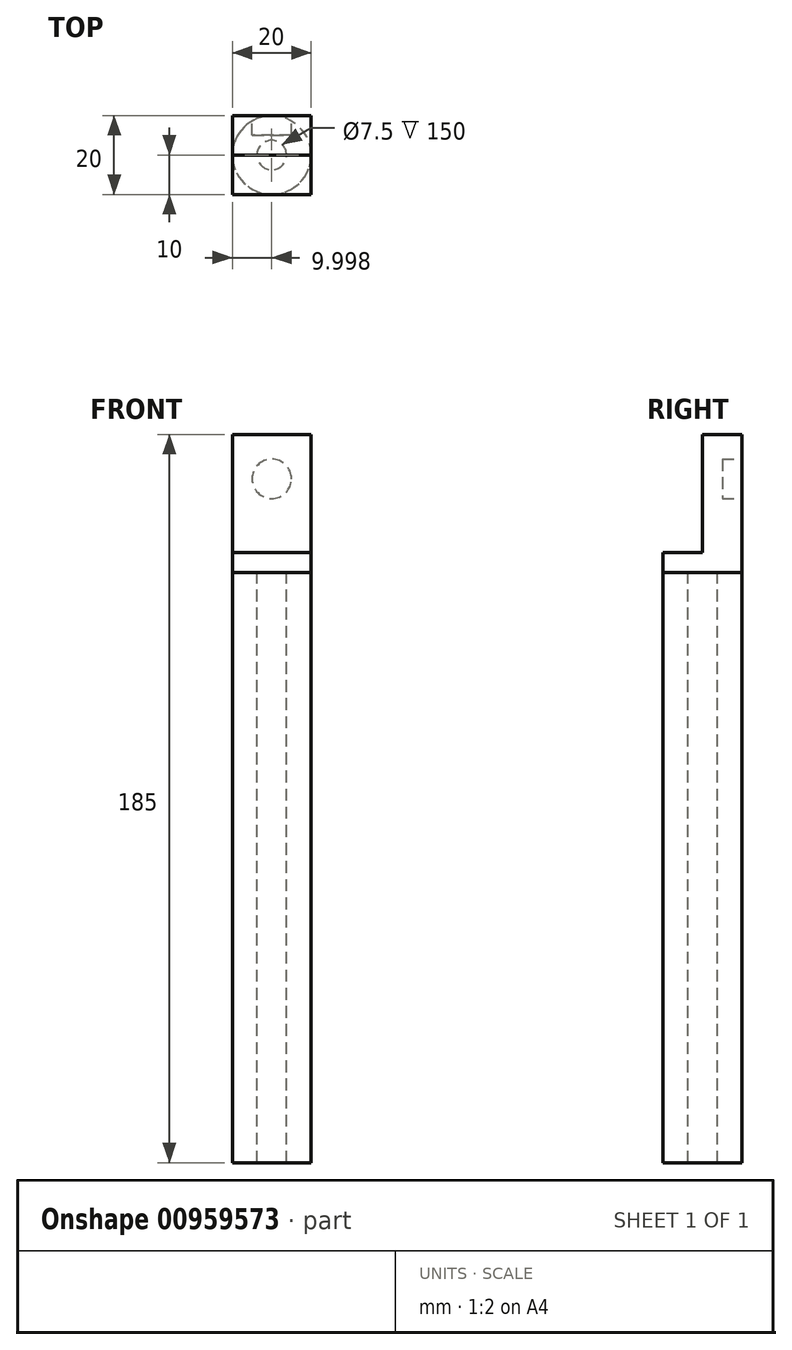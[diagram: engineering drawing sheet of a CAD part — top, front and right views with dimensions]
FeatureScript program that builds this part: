
annotation { "Feature Type Name" : "Feature", "Feature Type Description" : "" }
export const myFeature = defineFeature(function(context is Context, id is Id, definition is map)
    precondition{}
    {
        {
            var Q0;
            Q0=qCreatedBy(makeId("Top.planeOp"),FACE);
            var sketch = newSketch(context, id + "F0", { "sketchPlane" : qUnion([Q0])});
            skLineSegment(sketch, "E0", {"start": v(-66.14, 69.13) * mm, "end": v(-46.14, 69.13) * mm});
            skLineSegment(sketch, "E1", {"start": v(-66.14, 69.13) * mm, "end": v(-66.14, 49.13) * mm});
            skLineSegment(sketch, "E2", {"start": v(-66.14, 49.13) * mm, "end": v(-46.14, 49.13) * mm});
            skLineSegment(sketch, "E3", {"start": v(-46.14, 69.13) * mm, "end": v(-46.14, 49.13) * mm});
            skSolve(sketch);
        }
        {
            var Q0;
            Q0 = qSketchRegion(id + "F0", true);
            var Q1;
            Q1=makeQuery(id+"F0.imprint","IMPRINT",FACE,{"disambiguationData":[TD([[makeQuery(id+"F0.imprint","IMPRINT",EDGE,{"derivedFrom":sQuery(id+"F0.wireOp",EDGE,"E0")}),-1.0]])]});
            extrude(context, id + "F1", {"entities" : qUnion([Q0, Q1]), "depth" : 5 * mm, "offsetDistance" : 25 * mm});
        }
        {
            var Q0;
            Q0=makeQuery(id+"F1.opExtrude","CAP_FACE",FACE,{"disambiguationData":[OSD([sQuery(id+"F0.wireOp",EDGE,"E0"),sQuery(id+"F0.wireOp",EDGE,"E1"),sQuery(id+"F0.wireOp",EDGE,"E2"),sQuery(id+"F0.wireOp",EDGE,"E3")])],"isStart":true});
            var sketch = newSketch(context, id + "F2", { "sketchPlane" : qUnion([Q0])});
            skCircle(sketch, "E4", {"center": v(-56.14, -59.13) * mm, "radius": 10 * mm});
            skPoint(sketch, "E4.first.point", {"position": v(-56.14, -49.13) * mm});
            skPoint(sketch, "E4.second.point", {"position": v(-56.14, -69.13) * mm});
            skPoint(sketch, "E4.third.point", {"position": v(-46.14, -59.13) * mm});
            skCircle(sketch, "E5", {"center": v(-56.14, -59.13) * mm, "radius": 3.75 * mm});
            skSolve(sketch);
        }
        {
            var Q0;
            Q0=makeQuery(id+"F2.imprint","IMPRINT",FACE,{"disambiguationData":[TD([[makeQuery(id+"F2.imprint","IMPRINT",EDGE,{"derivedFrom":sQuery(id+"F2.wireOp",EDGE,"E5")}),-1.0]])]});
            extrude(context, id + "F3", {"entities" : qUnion([Q0]), "operationType" : NewBodyOperationType.ADD, "depth" : 150 * mm, "offsetDistance" : 25 * mm});
        }
        {
            var Q0;
            Q0=makeQuery(id+"F1.opExtrude","CAP_FACE",FACE,{"disambiguationData":[OSD([sQuery(id+"F0.wireOp",EDGE,"E0"),sQuery(id+"F0.wireOp",EDGE,"E1"),sQuery(id+"F0.wireOp",EDGE,"E2"),sQuery(id+"F0.wireOp",EDGE,"E3")])],"isStart":false});
            var sketch = newSketch(context, id + "F4", { "sketchPlane" : qUnion([Q0])});
            skLineSegment(sketch, "E6", {"start": v(-66.14, 69.13) * mm, "end": v(-46.14, 69.13) * mm});
            skLineSegment(sketch, "E7", {"start": v(-66.14, 59.13) * mm, "end": v(-46.14, 59.13) * mm});
            skLineSegment(sketch, "E8", {"start": v(-46.14, 59.13) * mm, "end": v(-46.14, 69.13) * mm});
            skLineSegment(sketch, "E9", {"start": v(-66.14, 69.13) * mm, "end": v(-66.14, 59.13) * mm});
            skSolve(sketch);
        }
        {
            var Q0;
            Q0=makeQuery(id+"F4.imprint","IMPRINT",FACE,{"disambiguationData":[TD([[makeQuery(id+"F4.imprint","IMPRINT",EDGE,{"derivedFrom":sQuery(id+"F4.wireOp",EDGE,"E6")}),-1.0]])]});
            extrude(context, id + "F5", {"entities" : qUnion([Q0]), "operationType" : NewBodyOperationType.ADD, "depth" : 30 * mm, "offsetDistance" : 25 * mm});
        }
        {
            var Q0;
            Q0=makeQuery(id+"F5.boolean.opBoolean","MERGE",FACE,{"derivedFrom":[makeQuery(id+"F1.opExtrude","SWEPT_FACE",FACE,{"disambiguationData":[OSD([sQuery(id+"F0.wireOp",EDGE,"E0")])]}),makeQuery(id+"F5.opExtrude","SWEPT_FACE",FACE,{"disambiguationData":[OSD([sQuery(id+"F4.wireOp",EDGE,"E6")])]})]});
            var sketch = newSketch(context, id + "F6", { "sketchPlane" : qUnion([Q0])});
            skPoint(sketch, "E10.start.orphan", {"position": v(46.14, 25) * mm});
            skPoint(sketch, "E11.orphan", {"position": v(66.14, 25) * mm});
            skPoint(sketch, "E12.start.orphan", {"position": v(66.14, 12.5) * mm});
            skPoint(sketch, "E13.start.orphan", {"position": v(66.14, 0) * mm});
            skPoint(sketch, "E14.end.orphan", {"position": v(46.14, 12.5) * mm});
            skPoint(sketch, "E14.start.orphan", {"position": v(46.14, 0) * mm});
            skLineSegment(sketch, "E15", {"start": v(46.14, 0) * mm, "end": v(46.14, 5) * mm});
            skLineSegment(sketch, "E16", {"start": v(46.14, 5) * mm, "end": v(66.14, 5) * mm});
            skLineSegment(sketch, "E17", {"start": v(66.14, 5) * mm, "end": v(66.14, 30) * mm});
            skLineSegment(sketch, "E18", {"start": v(46.14, 30) * mm, "end": v(46.14, 5) * mm});
            skCircle(sketch, "E19", {"center": v(56.14, 23.75) * mm, "radius": 5 * mm});
            skPoint(sketch, "E20.end.orphan", {"position": v(66.14, 17.5) * mm});
            skPoint(sketch, "E20.start.orphan", {"position": v(46.14, 17.5) * mm});
            skSolve(sketch);
        }
        {
            var Q0;
            Q0=makeQuery(id+"F6.imprint","IMPRINT",FACE,{"disambiguationData":[TD([[makeQuery(id+"F6.imprint","IMPRINT",EDGE,{"derivedFrom":sQuery(id+"F6.wireOp",EDGE,"E19")}),1.0]])]});
            extrude(context, id + "F7", {"entities" : qUnion([Q0]), "operationType" : NewBodyOperationType.REMOVE, "oppositeDirection" : true, "depth" : 5 * mm, "offsetDistance" : 25 * mm});
        }
    });
